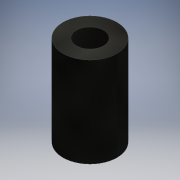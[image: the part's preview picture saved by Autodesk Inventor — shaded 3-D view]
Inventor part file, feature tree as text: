
AUTODESK INVENTOR PART (.ipt)
format: ipt  version: 2016 (Build 200138000, 138)  size: 94,208 bytes
history: native  units: mm
features: other x1, extrude x1, sketch x1
ambient origin geometry x8: Origin, YZ Plane, XZ Plane, XY Plane, X Axis, Y Axis, Z Axis, Center Point
bodies: Body1 (feature_tree)
feature tree (3):
  other  "ソリッド1"
  extrude  "押し出し1"  Depth=6.0mm
  sketch  "スケッチ1"
